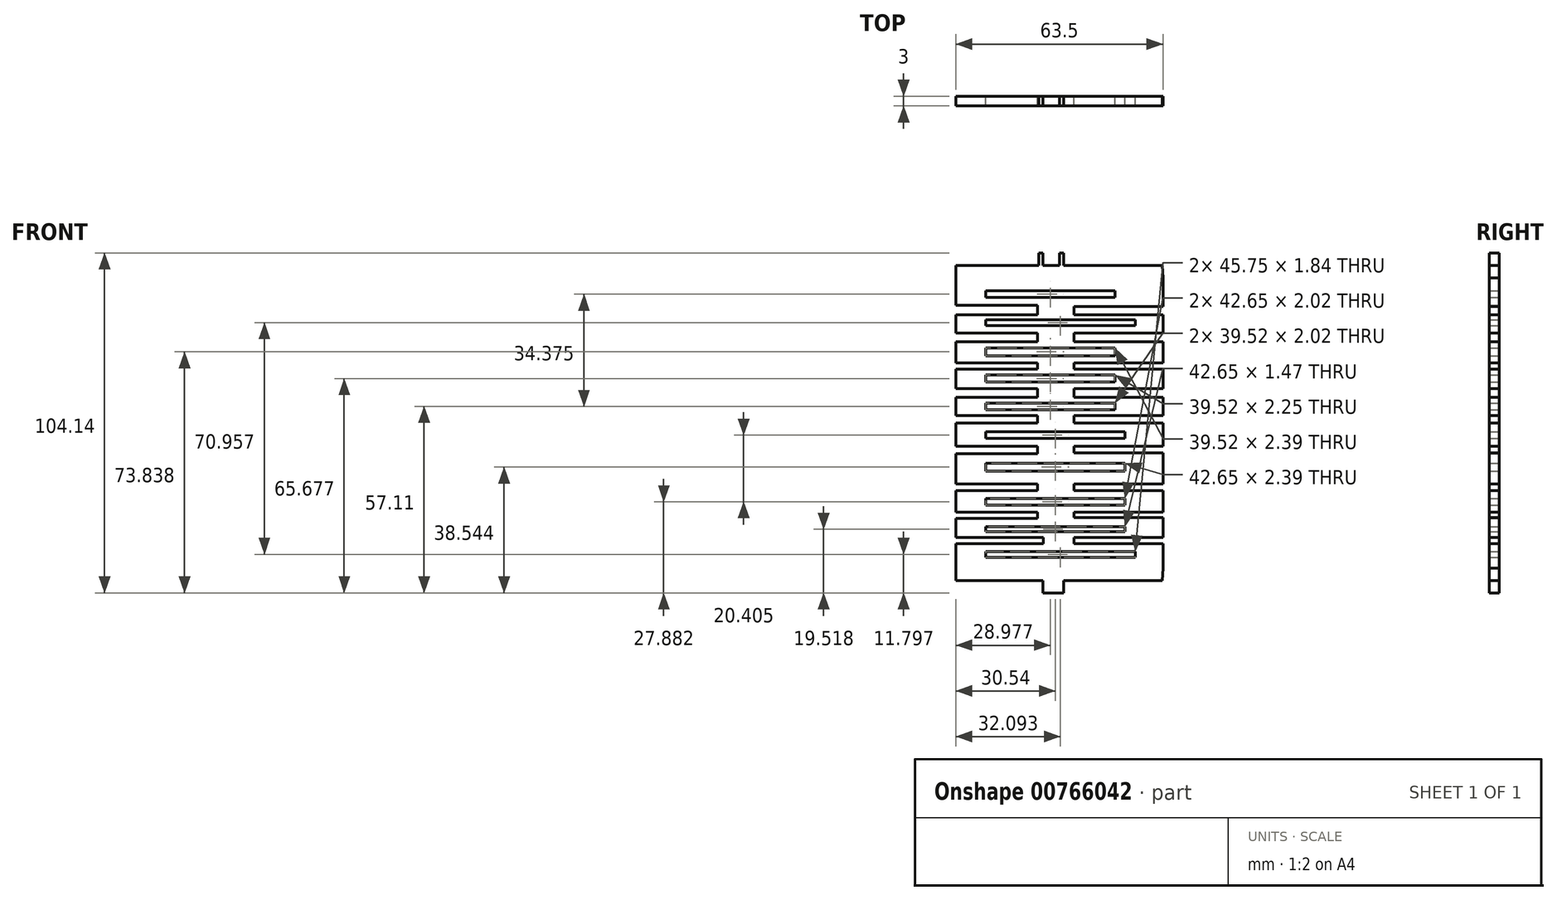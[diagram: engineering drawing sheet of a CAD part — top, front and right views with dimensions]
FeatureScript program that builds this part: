
annotation { "Feature Type Name" : "Feature", "Feature Type Description" : "" }
export const myFeature = defineFeature(function(context is Context, id is Id, definition is map)
    precondition{}
    {
        {
            var Q0;
            Q0=qCreatedBy(makeId("Front.planeOp"),FACE);
            var sketch = newSketch(context, id + "F0", { "sketchPlane" : qUnion([Q0])});
            skLineSegment(sketch, "E0.bottom", {"start": v(-54.97, 29.72) * mm, "end": v(8.53, 29.72) * mm});
            skLineSegment(sketch, "E0.top", {"start": v(-54.97, -59.18) * mm, "end": v(8.53, -59.18) * mm});
            skLineSegment(sketch, "E0.left", {"start": v(-54.97, 29.72) * mm, "end": v(-54.97, 21.28) * mm});
            skLineSegment(sketch, "E0.right", {"start": v(8.53, 29.72) * mm, "end": v(8.53, 20.92) * mm});
            skLineSegment(sketch, "E1.bottom", {"start": v(-45.75, -54.08) * mm, "end": v(0, -54.08) * mm});
            skLineSegment(sketch, "E1.top", {"start": v(-45.75, -55.92) * mm, "end": v(0, -55.92) * mm});
            skLineSegment(sketch, "E1.left", {"start": v(-45.75, -54.08) * mm, "end": v(-45.75, -55.92) * mm});
            skLineSegment(sketch, "E1.right", {"start": v(0, -54.08) * mm, "end": v(0, -55.92) * mm});
            skLineSegment(sketch, "E2.bottom", {"start": v(-54.97, -51.7) * mm, "end": v(-28.1, -51.7) * mm});
            skLineSegment(sketch, "E2.top", {"start": v(-54.97, -49.86) * mm, "end": v(-28.1, -49.86) * mm});
            skLineSegment(sketch, "E2.right", {"start": v(-28.1, -51.7) * mm, "end": v(-28.1, -49.86) * mm});
            skLineSegment(sketch, "E3.bottom", {"start": v(8.53, -49.86) * mm, "end": v(-18.73, -49.86) * mm});
            skLineSegment(sketch, "E3.top", {"start": v(8.53, -51.7) * mm, "end": v(-18.73, -51.7) * mm});
            skLineSegment(sketch, "E3.right", {"start": v(-18.73, -49.86) * mm, "end": v(-18.73, -51.7) * mm});
            skLineSegment(sketch, "E4.bottom", {"start": v(-45.75, -46.55) * mm, "end": v(-3.1, -46.55) * mm});
            skLineSegment(sketch, "E4.top", {"start": v(-45.75, -48.02) * mm, "end": v(-3.1, -48.02) * mm});
            skLineSegment(sketch, "E4.left", {"start": v(-45.75, -46.55) * mm, "end": v(-45.75, -48.02) * mm});
            skLineSegment(sketch, "E4.right", {"start": v(-3.1, -46.55) * mm, "end": v(-3.1, -48.02) * mm});
            skLineSegment(sketch, "E5.bottom", {"start": v(-18.73, -43.79) * mm, "end": v(8.53, -43.79) * mm});
            skLineSegment(sketch, "E5.top", {"start": v(-18.73, -42.14) * mm, "end": v(8.53, -42.14) * mm});
            skLineSegment(sketch, "E5.left", {"start": v(-18.73, -43.79) * mm, "end": v(-18.73, -42.14) * mm});
            skLineSegment(sketch, "E6.bottom", {"start": v(-29.95, -42.14) * mm, "end": v(-54.97, -42.14) * mm});
            skLineSegment(sketch, "E6.top", {"start": v(-29.95, -43.97) * mm, "end": v(-54.97, -43.97) * mm});
            skLineSegment(sketch, "E6.left", {"start": v(-29.95, -42.14) * mm, "end": v(-29.95, -43.97) * mm});
            skLineSegment(sketch, "E7.bottom", {"start": v(-45.75, -37.9) * mm, "end": v(-3.1, -37.9) * mm});
            skLineSegment(sketch, "E7.top", {"start": v(-45.75, -39.93) * mm, "end": v(-3.1, -39.93) * mm});
            skLineSegment(sketch, "E7.left", {"start": v(-45.75, -37.9) * mm, "end": v(-45.75, -39.93) * mm});
            skLineSegment(sketch, "E7.right", {"start": v(-3.1, -37.9) * mm, "end": v(-3.1, -39.93) * mm});
            skLineSegment(sketch, "E8.bottom", {"start": v(-29.95, -33.5) * mm, "end": v(-54.97, -33.5) * mm});
            skLineSegment(sketch, "E8.top", {"start": v(-29.95, -35.52) * mm, "end": v(-54.97, -35.52) * mm});
            skLineSegment(sketch, "E8.left", {"start": v(-29.95, -33.5) * mm, "end": v(-29.95, -35.52) * mm});
            skLineSegment(sketch, "E9.bottom", {"start": v(-18.73, -35.52) * mm, "end": v(8.53, -35.52) * mm});
            skLineSegment(sketch, "E9.top", {"start": v(-18.73, -33.5) * mm, "end": v(8.53, -33.5) * mm});
            skLineSegment(sketch, "E9.left", {"start": v(-18.73, -35.52) * mm, "end": v(-18.73, -33.5) * mm});
            skLineSegment(sketch, "E10.bottom", {"start": v(-45.75, -29.45) * mm, "end": v(-3.1, -29.45) * mm});
            skLineSegment(sketch, "E10.top", {"start": v(-45.75, -27.06) * mm, "end": v(-3.1, -27.06) * mm});
            skLineSegment(sketch, "E10.left", {"start": v(-45.75, -29.45) * mm, "end": v(-45.75, -27.06) * mm});
            skLineSegment(sketch, "E10.right", {"start": v(-3.1, -29.45) * mm, "end": v(-3.1, -27.06) * mm});
            skLineSegment(sketch, "E11.bottom", {"start": v(-18.73, -23.94) * mm, "end": v(8.53, -23.94) * mm});
            skLineSegment(sketch, "E11.top", {"start": v(-18.73, -21.91) * mm, "end": v(8.53, -21.91) * mm});
            skLineSegment(sketch, "E11.left", {"start": v(-18.73, -23.94) * mm, "end": v(-18.73, -21.91) * mm});
            skLineSegment(sketch, "E12.bottom", {"start": v(-29.95, -21.91) * mm, "end": v(-54.97, -21.91) * mm});
            skLineSegment(sketch, "E12.top", {"start": v(-29.95, -24.12) * mm, "end": v(-54.97, -24.12) * mm});
            skLineSegment(sketch, "E12.left", {"start": v(-29.95, -21.91) * mm, "end": v(-29.95, -24.12) * mm});
            skLineSegment(sketch, "E13.bottom", {"start": v(-45.75, -17.5) * mm, "end": v(-3.1, -17.5) * mm});
            skLineSegment(sketch, "E13.top", {"start": v(-45.75, -19.52) * mm, "end": v(-3.1, -19.52) * mm});
            skLineSegment(sketch, "E13.left", {"start": v(-45.75, -17.5) * mm, "end": v(-45.75, -19.52) * mm});
            skLineSegment(sketch, "E13.right", {"start": v(-3.1, -17.5) * mm, "end": v(-3.1, -19.52) * mm});
            skLineSegment(sketch, "E14.bottom", {"start": v(-18.73, -12.54) * mm, "end": v(8.53, -12.54) * mm});
            skLineSegment(sketch, "E14.top", {"start": v(-18.73, -14.73) * mm, "end": v(8.53, -14.73) * mm});
            skLineSegment(sketch, "E14.left", {"start": v(-18.73, -12.54) * mm, "end": v(-18.73, -14.73) * mm});
            skLineSegment(sketch, "E15.bottom", {"start": v(-29.95, -12.54) * mm, "end": v(-54.97, -12.54) * mm});
            skLineSegment(sketch, "E15.top", {"start": v(-29.95, -14.73) * mm, "end": v(-54.97, -14.73) * mm});
            skLineSegment(sketch, "E15.left", {"start": v(-29.95, -12.54) * mm, "end": v(-29.95, -14.73) * mm});
            skLineSegment(sketch, "E16.bottom", {"start": v(-45.75, -8.68) * mm, "end": v(-6.23, -8.68) * mm});
            skLineSegment(sketch, "E16.top", {"start": v(-45.75, -10.7) * mm, "end": v(-6.23, -10.7) * mm});
            skLineSegment(sketch, "E16.left", {"start": v(-45.75, -8.68) * mm, "end": v(-45.75, -10.7) * mm});
            skLineSegment(sketch, "E16.right", {"start": v(-6.23, -8.68) * mm, "end": v(-6.23, -10.7) * mm});
            skLineSegment(sketch, "E17.bottom", {"start": v(-18.73, -4.27) * mm, "end": v(8.53, -4.27) * mm});
            skLineSegment(sketch, "E17.top", {"start": v(-18.73, -6.84) * mm, "end": v(8.53, -6.84) * mm});
            skLineSegment(sketch, "E17.left", {"start": v(-18.73, -4.27) * mm, "end": v(-18.73, -6.84) * mm});
            skLineSegment(sketch, "E18.bottom", {"start": v(-29.95, -4.27) * mm, "end": v(-54.97, -4.27) * mm});
            skLineSegment(sketch, "E18.top", {"start": v(-29.95, -6.84) * mm, "end": v(-54.97, -6.84) * mm});
            skLineSegment(sketch, "E18.left", {"start": v(-29.95, -4.27) * mm, "end": v(-29.95, -6.84) * mm});
            skLineSegment(sketch, "E19.bottom", {"start": v(-45.75, 0) * mm, "end": v(-6.23, 0) * mm});
            skLineSegment(sketch, "E19.top", {"start": v(-45.75, -2.25) * mm, "end": v(-6.23, -2.25) * mm});
            skLineSegment(sketch, "E19.left", {"start": v(-45.75, 0) * mm, "end": v(-45.75, -2.25) * mm});
            skLineSegment(sketch, "E19.right", {"start": v(-6.23, 0) * mm, "end": v(-6.23, -2.25) * mm});
            skLineSegment(sketch, "E20.bottom", {"start": v(-18.73, 3.64) * mm, "end": v(8.53, 3.64) * mm});
            skLineSegment(sketch, "E20.top", {"start": v(-18.73, 1.8) * mm, "end": v(8.53, 1.8) * mm});
            skLineSegment(sketch, "E20.left", {"start": v(-18.73, 3.64) * mm, "end": v(-18.73, 1.8) * mm});
            skLineSegment(sketch, "E21.bottom", {"start": v(-29.95, 3.64) * mm, "end": v(-54.97, 3.64) * mm});
            skLineSegment(sketch, "E21.top", {"start": v(-29.95, 1.8) * mm, "end": v(-54.97, 1.8) * mm});
            skLineSegment(sketch, "E21.left", {"start": v(-29.95, 3.64) * mm, "end": v(-29.95, 1.8) * mm});
            skLineSegment(sketch, "E22.bottom", {"start": v(-45.75, 8.23) * mm, "end": v(-6.23, 8.23) * mm});
            skLineSegment(sketch, "E22.top", {"start": v(-45.75, 5.84) * mm, "end": v(-6.23, 5.84) * mm});
            skLineSegment(sketch, "E22.left", {"start": v(-45.75, 8.23) * mm, "end": v(-45.75, 5.84) * mm});
            skLineSegment(sketch, "E22.right", {"start": v(-6.23, 8.23) * mm, "end": v(-6.23, 5.84) * mm});
            skLineSegment(sketch, "E23.bottom", {"start": v(-18.73, 12.83) * mm, "end": v(8.53, 12.83) * mm});
            skLineSegment(sketch, "E23.top", {"start": v(-18.73, 10.07) * mm, "end": v(8.53, 10.07) * mm});
            skLineSegment(sketch, "E23.left", {"start": v(-18.73, 12.83) * mm, "end": v(-18.73, 10.07) * mm});
            skLineSegment(sketch, "E24.bottom", {"start": v(-29.95, 12.83) * mm, "end": v(-54.97, 12.83) * mm});
            skLineSegment(sketch, "E24.top", {"start": v(-29.95, 10.07) * mm, "end": v(-54.97, 10.07) * mm});
            skLineSegment(sketch, "E24.left", {"start": v(-29.95, 12.83) * mm, "end": v(-29.95, 10.07) * mm});
            skLineSegment(sketch, "E25.bottom", {"start": v(-45.75, 16.87) * mm, "end": v(0, 16.87) * mm});
            skLineSegment(sketch, "E25.top", {"start": v(-45.75, 15.03) * mm, "end": v(0, 15.03) * mm});
            skLineSegment(sketch, "E25.left", {"start": v(-45.75, 16.87) * mm, "end": v(-45.75, 15.03) * mm});
            skLineSegment(sketch, "E25.right", {"start": v(0, 16.87) * mm, "end": v(0, 15.03) * mm});
            skLineSegment(sketch, "E26.bottom", {"start": v(-29.95, 21.28) * mm, "end": v(-54.97, 21.28) * mm});
            skLineSegment(sketch, "E26.top", {"start": v(-29.95, 18.34) * mm, "end": v(-54.97, 18.34) * mm});
            skLineSegment(sketch, "E26.left", {"start": v(-29.95, 21.28) * mm, "end": v(-29.95, 18.34) * mm});
            skLineSegment(sketch, "E27.bottom", {"start": v(-18.73, 20.92) * mm, "end": v(8.53, 20.92) * mm});
            skLineSegment(sketch, "E27.top", {"start": v(-18.73, 18.34) * mm, "end": v(8.53, 18.34) * mm});
            skLineSegment(sketch, "E27.left", {"start": v(-18.73, 20.92) * mm, "end": v(-18.73, 18.34) * mm});
            skLineSegment(sketch, "E28.bottom", {"start": v(-45.75, 25.7) * mm, "end": v(-6.23, 25.7) * mm});
            skLineSegment(sketch, "E28.top", {"start": v(-45.75, 23.67) * mm, "end": v(-6.23, 23.67) * mm});
            skLineSegment(sketch, "E28.left", {"start": v(-45.75, 25.7) * mm, "end": v(-45.75, 23.67) * mm});
            skLineSegment(sketch, "E28.right", {"start": v(-6.23, 25.7) * mm, "end": v(-6.23, 23.67) * mm});
            skLineSegment(sketch, "E29", {"start": v(-54.97, 29.72) * mm, "end": v(-54.97, 33.53) * mm});
            skLineSegment(sketch, "E30", {"start": v(-54.97, 33.53) * mm, "end": v(-29.57, 33.53) * mm});
            skLineSegment(sketch, "E31", {"start": v(-29.57, 33.53) * mm, "end": v(-29.57, 37.34) * mm});
            skLineSegment(sketch, "E32", {"start": v(-29.57, 37.34) * mm, "end": v(-28.3, 37.34) * mm});
            skLineSegment(sketch, "E33", {"start": v(-28.3, 37.34) * mm, "end": v(-28.3, 33.53) * mm});
            skLineSegment(sketch, "E34", {"start": v(-28.3, 33.53) * mm, "end": v(-23.22, 33.53) * mm});
            skLineSegment(sketch, "E35", {"start": v(-23.22, 33.53) * mm, "end": v(-23.22, 37.34) * mm});
            skLineSegment(sketch, "E36", {"start": v(-23.22, 37.34) * mm, "end": v(-21.95, 37.34) * mm});
            skLineSegment(sketch, "E37", {"start": v(-21.95, 37.34) * mm, "end": v(-21.95, 33.53) * mm});
            skLineSegment(sketch, "E38", {"start": v(-21.95, 33.53) * mm, "end": v(8.3, 33.53) * mm});
            skLineSegment(sketch, "E39", {"start": v(8.3, 33.53) * mm, "end": v(8.53, 29.72) * mm});
            skLineSegment(sketch, "E40", {"start": v(-54.97, -59.18) * mm, "end": v(-54.97, -62.99) * mm});
            skLineSegment(sketch, "E41", {"start": v(-54.97, -62.99) * mm, "end": v(-28.3, -62.99) * mm});
            skLineSegment(sketch, "E42", {"start": v(-28.3, -62.99) * mm, "end": v(-28.3, -66.8) * mm});
            skLineSegment(sketch, "E43", {"start": v(-28.3, -66.8) * mm, "end": v(-21.95, -66.8) * mm});
            skLineSegment(sketch, "E44", {"start": v(-21.95, -66.8) * mm, "end": v(-21.95, -62.99) * mm});
            skLineSegment(sketch, "E45", {"start": v(-21.95, -62.99) * mm, "end": v(8.3, -62.99) * mm});
            skLineSegment(sketch, "E46", {"start": v(8.3, -62.99) * mm, "end": v(8.53, -59.18) * mm});
            skLineSegment(sketch, "E47.trimOffspring", {"start": v(8.53, 18.34) * mm, "end": v(8.53, 12.83) * mm});
            skLineSegment(sketch, "E48.trimOffspring", {"start": v(8.53, 10.07) * mm, "end": v(8.53, 3.64) * mm});
            skLineSegment(sketch, "E49.trimOffspring", {"start": v(8.53, 1.8) * mm, "end": v(8.53, -4.27) * mm});
            skLineSegment(sketch, "E50.trimOffspring", {"start": v(8.53, -6.84) * mm, "end": v(8.53, -12.54) * mm});
            skLineSegment(sketch, "E51.trimOffspring", {"start": v(8.53, -14.73) * mm, "end": v(8.53, -21.91) * mm});
            skLineSegment(sketch, "E52.trimOffspring", {"start": v(8.53, -23.94) * mm, "end": v(8.53, -33.5) * mm});
            skLineSegment(sketch, "E53.trimOffspring", {"start": v(8.53, -35.52) * mm, "end": v(8.53, -42.14) * mm});
            skLineSegment(sketch, "E54.trimOffspring", {"start": v(8.53, -43.79) * mm, "end": v(8.53, -49.86) * mm});
            skLineSegment(sketch, "E55.trimOffspring", {"start": v(8.53, -51.7) * mm, "end": v(8.53, -59.18) * mm});
            skLineSegment(sketch, "E56.trimOffspring", {"start": v(-54.97, -51.7) * mm, "end": v(-54.97, -59.18) * mm});
            skLineSegment(sketch, "E57.trimOffspring", {"start": v(-54.97, -43.97) * mm, "end": v(-54.97, -49.86) * mm});
            skLineSegment(sketch, "E58.trimOffspring", {"start": v(-54.97, -35.52) * mm, "end": v(-54.97, -42.14) * mm});
            skLineSegment(sketch, "E59.trimOffspring", {"start": v(-54.97, -24.12) * mm, "end": v(-54.97, -33.5) * mm});
            skLineSegment(sketch, "E60.trimOffspring", {"start": v(-54.97, -14.73) * mm, "end": v(-54.97, -21.91) * mm});
            skLineSegment(sketch, "E61.trimOffspring", {"start": v(-54.97, -6.84) * mm, "end": v(-54.97, -12.54) * mm});
            skLineSegment(sketch, "E62.trimOffspring", {"start": v(-54.97, 1.8) * mm, "end": v(-54.97, -4.27) * mm});
            skLineSegment(sketch, "E63.trimOffspring", {"start": v(-54.97, 10.07) * mm, "end": v(-54.97, 3.64) * mm});
            skLineSegment(sketch, "E64.trimOffspring", {"start": v(-54.97, 18.34) * mm, "end": v(-54.97, 12.83) * mm});
            skSolve(sketch);
        }
        {
            var Q0;
            Q0 = qSketchRegion(id + "F0", true);
            extrude(context, id + "F1", {"entities" : qUnion([Q0]), "depth" : 3 * mm, "offsetDistance" : 25 * mm});
        }
    });
